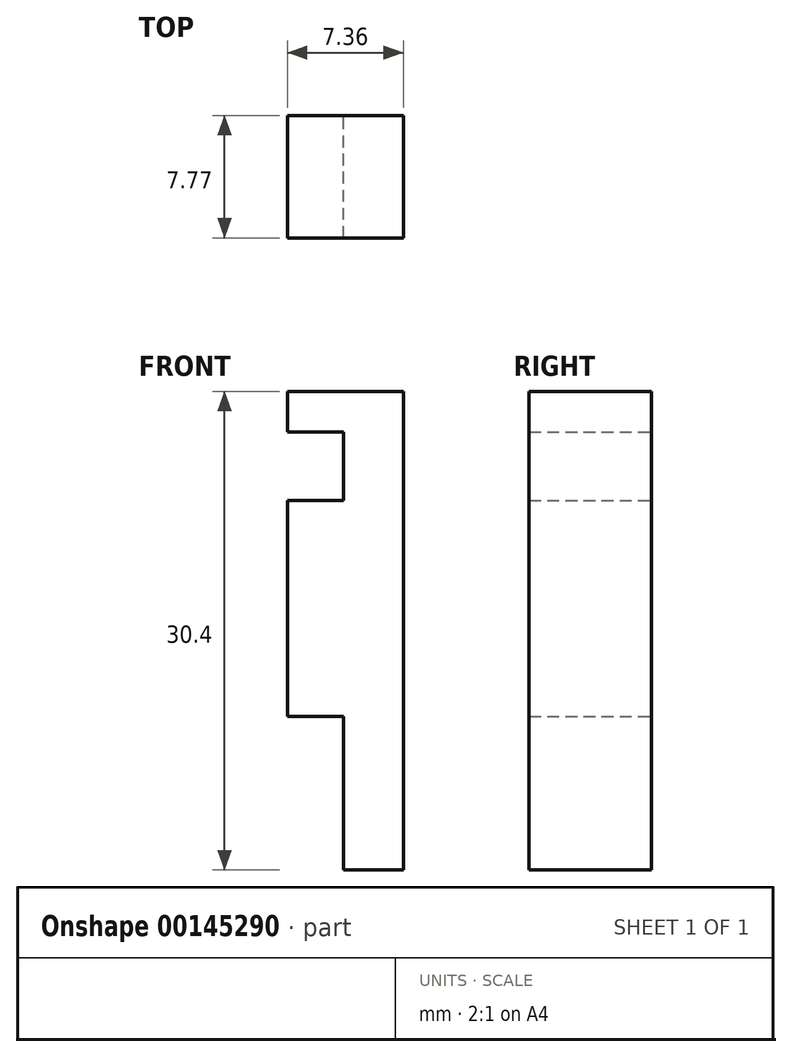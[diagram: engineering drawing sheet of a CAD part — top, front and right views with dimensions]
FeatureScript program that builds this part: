
annotation { "Feature Type Name" : "Feature", "Feature Type Description" : "" }
export const myFeature = defineFeature(function(context is Context, id is Id, definition is map)
    precondition{}
    {
        {
            var Q0;
            Q0=qCreatedBy(makeId("Front.planeOp"),FACE);
            var sketch = newSketch(context, id + "F0", { "sketchPlane" : qUnion([Q0])});
            skLineSegment(sketch, "E0", {"start": v(24.53, 9.05) * mm, "end": v(24.53, -21.35) * mm});
            skLineSegment(sketch, "E1", {"start": v(24.53, -21.35) * mm, "end": v(20.72, -21.35) * mm});
            skLineSegment(sketch, "E2", {"start": v(20.72, -21.35) * mm, "end": v(20.72, -11.6) * mm});
            skLineSegment(sketch, "E3", {"start": v(20.72, -11.6) * mm, "end": v(17.17, -11.6) * mm});
            skLineSegment(sketch, "E4", {"start": v(17.17, -11.6) * mm, "end": v(17.17, 2.11) * mm});
            skLineSegment(sketch, "E5", {"start": v(17.17, 2.11) * mm, "end": v(20.72, 2.11) * mm});
            skLineSegment(sketch, "E6", {"start": v(20.72, 2.11) * mm, "end": v(20.72, 6.48) * mm});
            skLineSegment(sketch, "E7", {"start": v(20.72, 6.48) * mm, "end": v(17.17, 6.48) * mm});
            skLineSegment(sketch, "E8", {"start": v(17.17, 6.48) * mm, "end": v(17.17, 9.05) * mm});
            skLineSegment(sketch, "E9", {"start": v(17.17, 9.05) * mm, "end": v(24.53, 9.05) * mm});
            skSolve(sketch);
        }
        {
            var Q0;
            Q0=makeQuery(id+"F0.imprint","IMPRINT",FACE,{"disambiguationData":[TD([[makeQuery(id+"F0.imprint","IMPRINT",EDGE,{"derivedFrom":sQuery(id+"F0.wireOp",EDGE,"E0")}),-1.0]])]});
            extrude(context, id + "F1", {"entities" : qUnion([Q0]), "depth" : 7.77 * mm});
        }
    });
